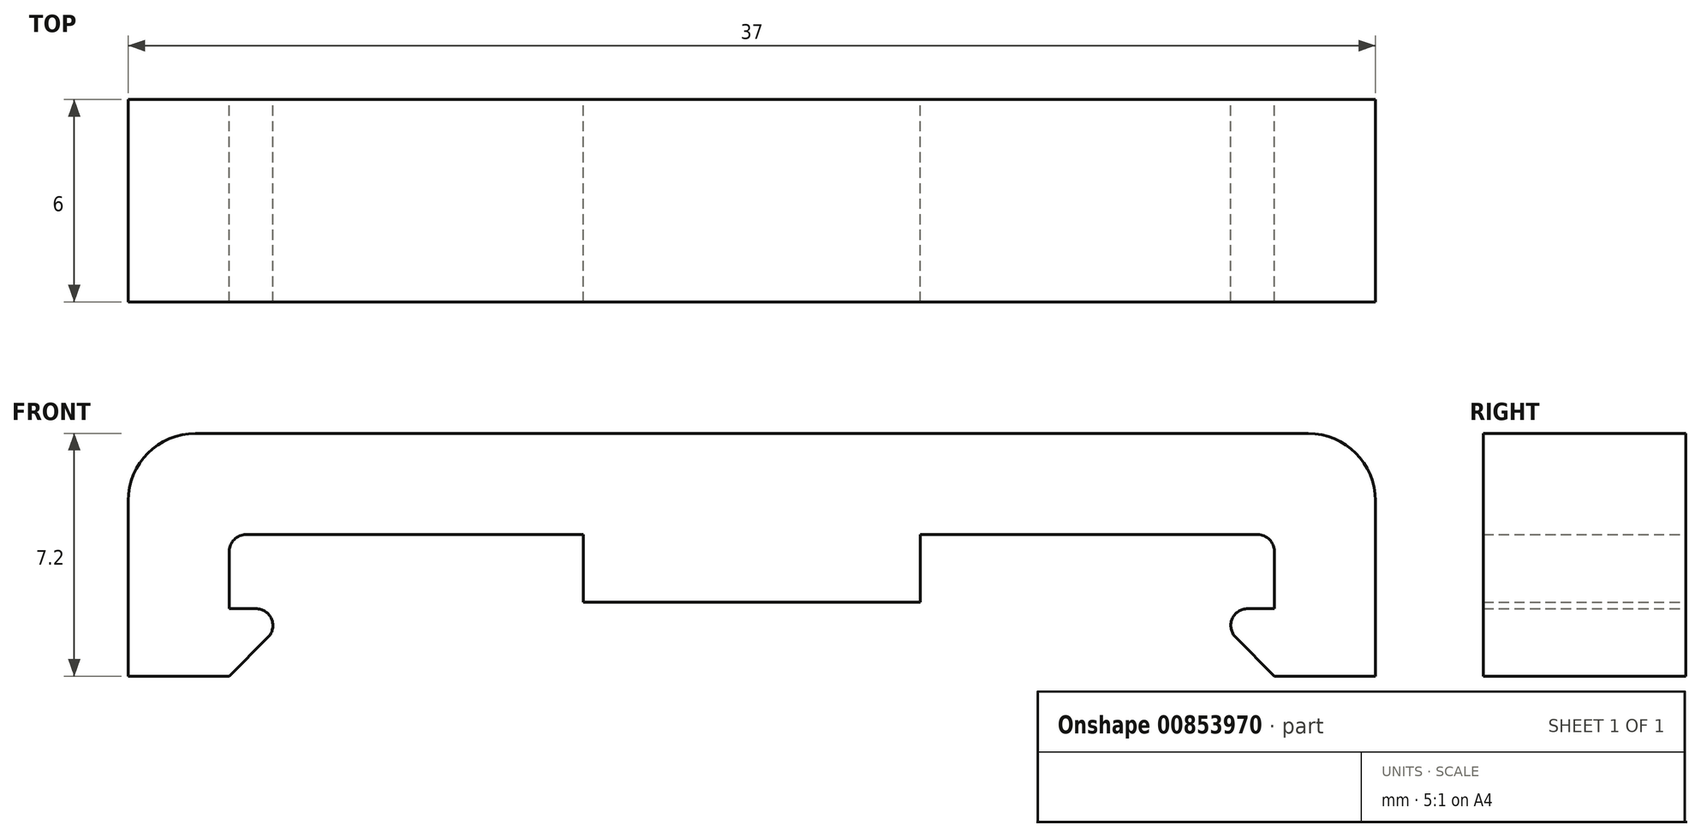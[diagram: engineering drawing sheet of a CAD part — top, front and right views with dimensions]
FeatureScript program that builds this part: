
annotation { "Feature Type Name" : "Feature", "Feature Type Description" : "" }
export const myFeature = defineFeature(function(context is Context, id is Id, definition is map)
    precondition{}
    {
        {
            var Q0;
            Q0=qCreatedBy(makeId("Front.planeOp"),FACE);
            var sketch = newSketch(context, id + "F0", { "sketchPlane" : qUnion([Q0])});
            skLineSegment(sketch, "E0", {"start": v(-18.5, 0) * mm, "end": v(18.5, 0) * mm});
            skLineSegment(sketch, "E1", {"start": v(-18.5, 0) * mm, "end": v(-18.5, -7.2) * mm});
            skLineSegment(sketch, "E2", {"start": v(-18.5, -7.2) * mm, "end": v(-15.5, -7.2) * mm});
            skLineSegment(sketch, "E3", {"start": v(-15.5, -7.2) * mm, "end": v(-13.5, -5.2) * mm});
            skLineSegment(sketch, "E4", {"start": v(-13.5, -5.2) * mm, "end": v(-15.5, -5.2) * mm});
            skLineSegment(sketch, "E5", {"start": v(-15.5, -5.2) * mm, "end": v(-15.5, -3) * mm});
            skLineSegment(sketch, "E6", {"start": v(18.5, 0) * mm, "end": v(18.5, -7.2) * mm});
            skLineSegment(sketch, "E7", {"start": v(18.5, -7.2) * mm, "end": v(15.5, -7.2) * mm});
            skLineSegment(sketch, "E8", {"start": v(15.5, -7.2) * mm, "end": v(13.5, -5.2) * mm});
            skLineSegment(sketch, "E9", {"start": v(13.5, -5.2) * mm, "end": v(15.5, -5.2) * mm});
            skLineSegment(sketch, "E10", {"start": v(15.5, -5.2) * mm, "end": v(15.5, -3) * mm});
            skLineSegment(sketch, "E11", {"start": v(15.5, -3) * mm, "end": v(-15.5, -3) * mm});
            skLineSegment(sketch, "E12", {"start": v(-5, -3) * mm, "end": v(-5, -5) * mm});
            skLineSegment(sketch, "E13", {"start": v(-5, -5) * mm, "end": v(5, -5) * mm});
            skLineSegment(sketch, "E14", {"start": v(5, -5) * mm, "end": v(5, -3) * mm});
            skPoint(sketch, "E15", {"position": v(0, -5) * mm});
            skSolve(sketch);
        }
        {
            var Q0;
            Q0=makeQuery(id+"F0.imprint","IMPRINT",FACE,{"disambiguationData":[TD([[makeQuery(id+"F0.imprint","IMPRINT",EDGE,{"derivedFrom":sQuery(id+"F0.wireOp",EDGE,"E0")}),-1.0]])]});
            var Q1;
            {var subQ0=sQuery(id+"F0.wireOp",EDGE,"E12");Q1=makeQuery(id+"F0.imprint","IMPRINT",FACE,{"disambiguationData":[TD([[makeQuery(id+"F0.imprint","IMPRINT",EDGE,{"derivedFrom":subQ0}),1.0]])]});}
            extrude(context, id + "F1", {"entities" : qUnion([Q0, Q1]), "endBound" : BoundingType.SYMMETRIC, "depth" : 6 * mm, "offsetDistance" : 25 * mm});
        }
        {
            var Q0;
            Q0=makeQuery(id+"F1.opExtrude","SWEPT_EDGE",EDGE,{"disambiguationData":[OSD([sQuery(id+"F0.wireOp",EDGE,"E0"),sQuery(id+"F0.wireOp",EDGE,"E6")])]});
            var Q1;
            Q1=makeQuery(id+"F1.opExtrude","SWEPT_EDGE",EDGE,{"disambiguationData":[OSD([sQuery(id+"F0.wireOp",EDGE,"E0"),sQuery(id+"F0.wireOp",EDGE,"E1")])]});
            fillet(context, id + "F2", {"entities" : qUnion([Q0, Q1]), "radius" : 2 * mm, "tangentPropagation" : true, "allowEdgeOverflow" : false});
        }
        {
            var Q0;
            Q0=makeQuery(id+"F1.opExtrude","SWEPT_EDGE",EDGE,{"disambiguationData":[OSD([sQuery(id+"F0.wireOp",EDGE,"E10"),sQuery(id+"F0.wireOp",EDGE,"E11")])]});
            var Q1;
            Q1=makeQuery(id+"F1.opExtrude","SWEPT_EDGE",EDGE,{"disambiguationData":[OSD([sQuery(id+"F0.wireOp",EDGE,"E5"),sQuery(id+"F0.wireOp",EDGE,"E11")])]});
            fillet(context, id + "F3", {"entities" : qUnion([Q0, Q1]), "radius" : 0.5 * mm, "tangentPropagation" : true, "allowEdgeOverflow" : false});
        }
        {
            var Q0;
            Q0=makeQuery(id+"F1.opExtrude","SWEPT_EDGE",EDGE,{"disambiguationData":[OSD([sQuery(id+"F0.wireOp",EDGE,"E8"),sQuery(id+"F0.wireOp",EDGE,"E9")])]});
            var Q1;
            Q1=makeQuery(id+"F1.opExtrude","SWEPT_EDGE",EDGE,{"disambiguationData":[OSD([sQuery(id+"F0.wireOp",EDGE,"E3"),sQuery(id+"F0.wireOp",EDGE,"E4")])]});
            fillet(context, id + "F4", {"entities" : qUnion([Q0, Q1]), "radius" : 0.5 * mm, "tangentPropagation" : true, "allowEdgeOverflow" : false});
        }
    });
